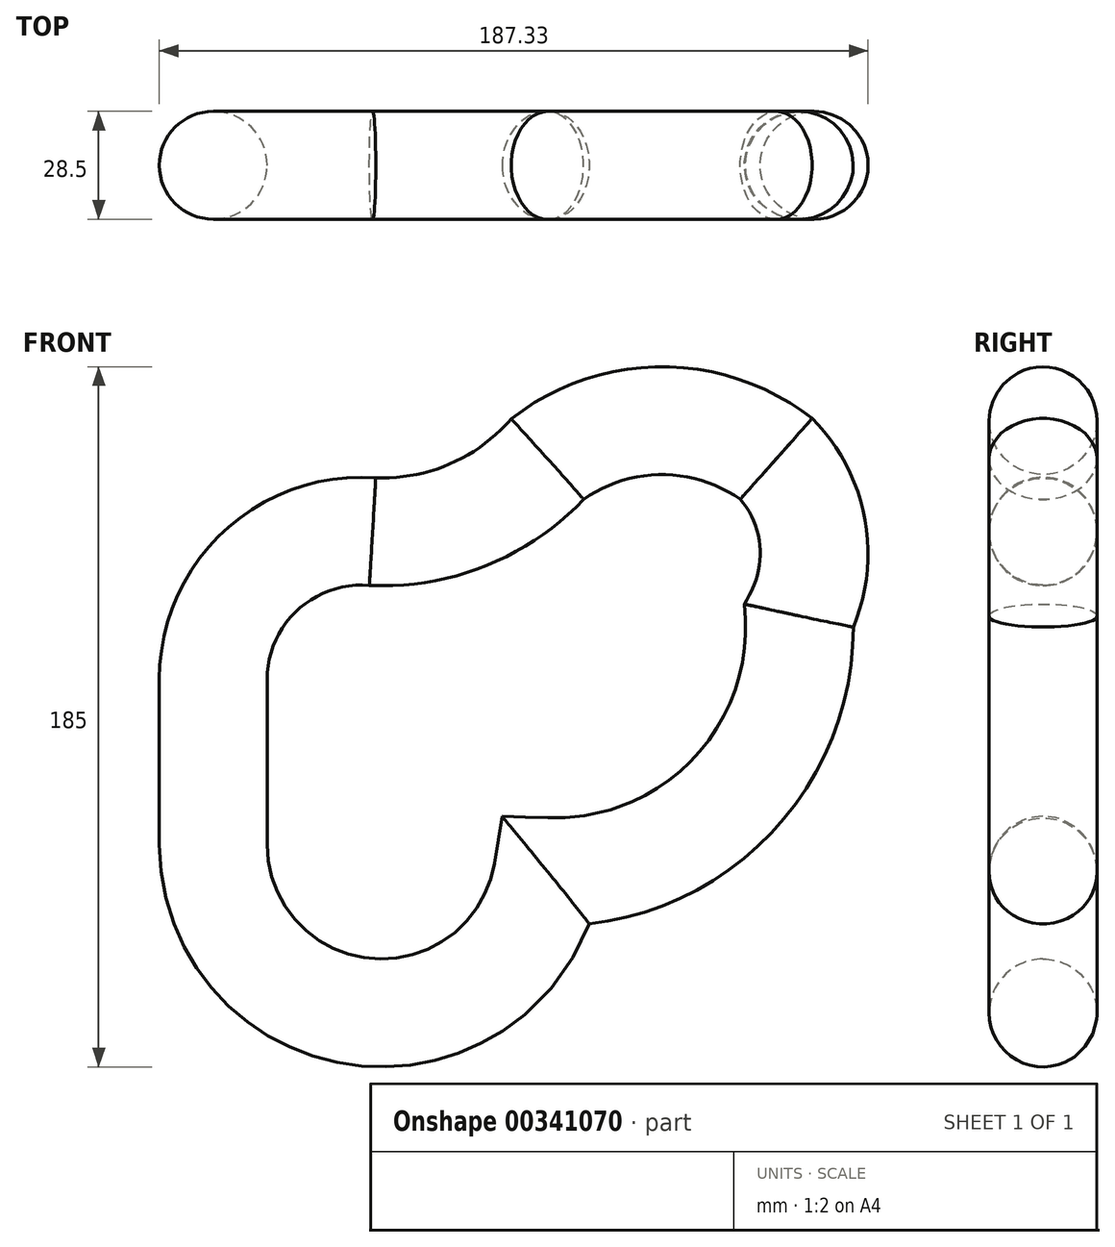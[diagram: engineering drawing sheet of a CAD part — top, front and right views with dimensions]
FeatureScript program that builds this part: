
annotation { "Feature Type Name" : "Feature", "Feature Type Description" : "" }
export const myFeature = defineFeature(function(context is Context, id is Id, definition is map)
    precondition{}
    {
        {
            var Q0;
            Q0=qCreatedBy(makeId("Front.planeOp"),FACE);
            var sketch = newSketch(context, id + "F0", { "sketchPlane" : qUnion([Q0])});
            skLineSegment(sketch, "E0", {"start": v(0, 0) * mm, "end": v(0, 43.65) * mm});
            skArc(sketch, "E1", {"start": v(42.13, 82.73) * mm, "mid": v(12.54, 72.38) * mm, "end": v(0, 43.65) * mm});
            skArc(sketch, "E2", {"start": v(42.13, 82.73) * mm, "mid": v(67.4, 87.18) * mm, "end": v(88.38, 101.95) * mm});
            skArc(sketch, "E3", {"start": v(148.82, 101.95) * mm, "mid": v(118.6, 112.03) * mm, "end": v(88.38, 101.95) * mm});
            skArc(sketch, "E4", {"start": v(154.84, 60.45) * mm, "mid": v(158.46, 82.16) * mm, "end": v(148.82, 101.95) * mm});
            skArc(sketch, "E5", {"start": v(88.38, -7.14) * mm, "mid": v(136.42, 12.09) * mm, "end": v(154.84, 60.45) * mm});
            skArc(sketch, "E6", {"start": v(0, 0) * mm, "mid": v(40.9, -44.34) * mm, "end": v(88.38, -7.14) * mm});
            skSolve(sketch);
        }
        {
            var Q0;
            Q0=qCreatedBy(makeId("Top.planeOp"),FACE);
            var sketch = newSketch(context, id + "F1", { "sketchPlane" : qUnion([Q0])});
            skCircle(sketch, "E7", {"center": v(0, 0) * mm, "radius": 14.25 * mm});
            skSolve(sketch);
        }
        {
            var Q0;
            Q0=makeQuery(id+"F1.imprint","IMPRINT",FACE,{"disambiguationData":[TD([[makeQuery(id+"F1.imprint","IMPRINT",EDGE,{"derivedFrom":sQuery(id+"F1.wireOp",EDGE,"E7")}),1.0]])]});
            var Q1;
            Q1 = qConstructionFilter(qBodyType(qCreatedBy(id + "F0" ,EDGE), BodyType.WIRE), ConstructionObject.NO);
            sweep(context, id + "F2", {"profiles" : qUnion([Q0]), "path" : qUnion([Q1])});
        }
    });
